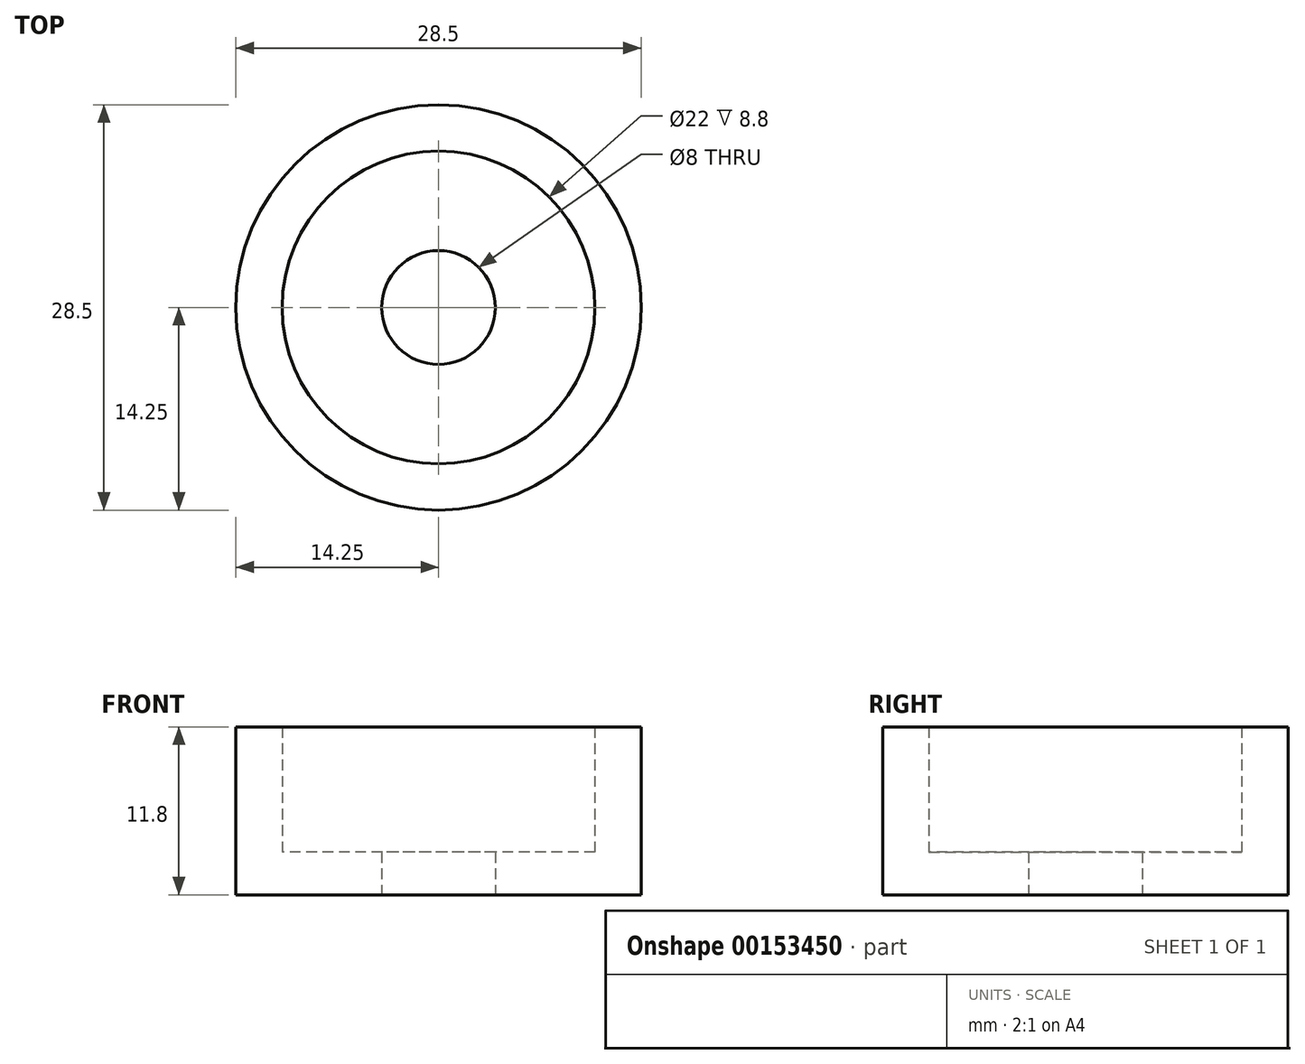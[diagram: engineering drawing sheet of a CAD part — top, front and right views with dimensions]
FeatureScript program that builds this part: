
annotation { "Feature Type Name" : "Feature", "Feature Type Description" : "" }
export const myFeature = defineFeature(function(context is Context, id is Id, definition is map)
    precondition{}
    {
        {
            var Q0;
            Q0=qCreatedBy(makeId("Top.planeOp"),FACE);
            var sketch = newSketch(context, id + "F0", { "sketchPlane" : qUnion([Q0])});
            skCircle(sketch, "E0", {"center": v(0, 0) * mm, "radius": 14.25 * mm});
            skCircle(sketch, "E1", {"center": v(0, 0) * mm, "radius": 11 * mm});
            skCircle(sketch, "E2", {"center": v(0, 0) * mm, "radius": 4 * mm});
            skSolve(sketch);
        }
        {
            var Q0;
            Q0 = qSketchRegion(id + "F0", true);
            extrude(context, id + "F1", {"entities" : qUnion([Q0]), "depth" : 11.8 * mm});
        }
        {
            var Q0;
            Q0=makeQuery(id+"F0.imprint","IMPRINT",FACE,{"disambiguationData":[TD([[makeQuery(id+"F0.imprint","IMPRINT",EDGE,{"derivedFrom":sQuery(id+"F0.wireOp",EDGE,"E0")}),1.0]])]});
            var Q1;
            Q1=makeQuery(id+"F0.imprint","IMPRINT",FACE,{"disambiguationData":[TD([[makeQuery(id+"F0.imprint","IMPRINT",EDGE,{"derivedFrom":sQuery(id+"F0.wireOp",EDGE,"E1")}),1.0]])]});
            extrude(context, id + "F2", {"entities" : qUnion([Q0, Q1]), "operationType" : NewBodyOperationType.ADD, "depth" : (11.8 - 1.8 - 7) * mm});
        }
    });
